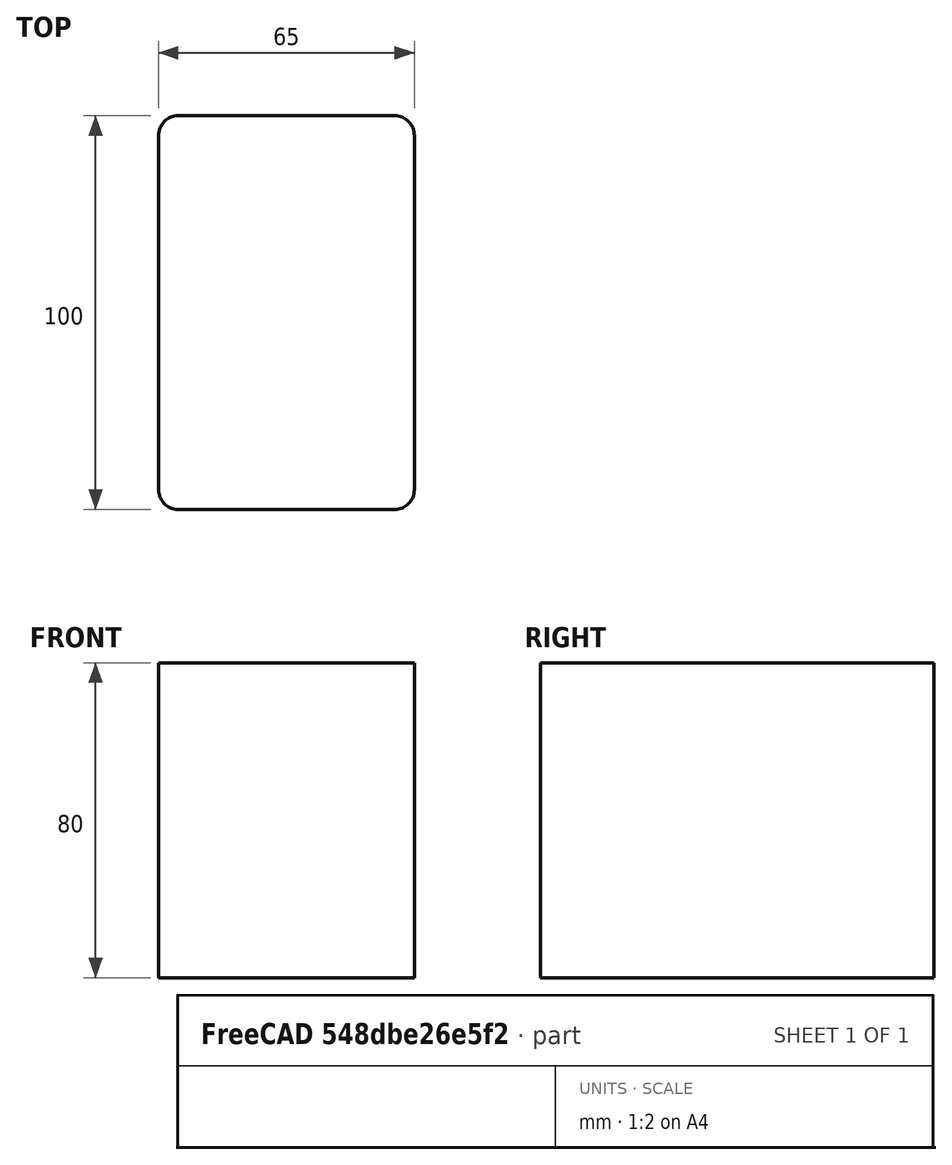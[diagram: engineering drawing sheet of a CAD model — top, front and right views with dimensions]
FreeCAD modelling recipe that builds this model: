
FCSTD DOCUMENT  (FreeCAD 0.22R37841 (Git))
Label: PrintheadCover
License: All rights reserved
LicenseURL: http://en.wikipedia.org/wiki/All_rights_reserved
objects: Mesh::Feature×8, Sketcher::SketchObject×2, PartDesign::Pad×1, PartDesign::Body×1
note: 5 computed .brp shape members not serialized (recipe doc carries the construction recipe); baked Part::Feature solids carry a one-line shape summary decoded from their .brp

FEATURE [Sketcher::SketchObject] Sketch
  AttachmentSupport = -> [XY_Plane]
  FullyConstrained = true
  MapMode = 5
  sketch-geometry (12):
    g0: LineSegment StartX=-32.5 StartY=45 StartZ=0 EndX=-32.5 EndY=-45 EndZ=0
    g1: LineSegment StartX=-27.5 StartY=-50 StartZ=0 EndX=27.5 EndY=-50 EndZ=0
    g2: LineSegment StartX=32.5 StartY=-45 StartZ=0 EndX=32.5 EndY=45 EndZ=0
    g3: LineSegment StartX=27.5 StartY=50 StartZ=0 EndX=-27.5 EndY=50 EndZ=0
    g4: ArcOfCircle CenterX=-27.5 CenterY=45 CenterZ=0 NormalX=0 NormalY=0 NormalZ=1 AngleXU=0 Radius=5 StartAngle=1.5708 EndAngle=3.14159
    g5: GeomPoint X=-32.5 Y=50 Z=0
    g6: ArcOfCircle CenterX=-27.5 CenterY=-45 CenterZ=0 NormalX=0 NormalY=0 NormalZ=1 AngleXU=0 Radius=5 StartAngle=3.14159 EndAngle=4.71239
    g7: GeomPoint X=-32.5 Y=-50 Z=0
    g8: ArcOfCircle CenterX=27.5 CenterY=-45 CenterZ=0 NormalX=0 NormalY=0 NormalZ=1 AngleXU=0 Radius=5 StartAngle=4.71239 EndAngle=6.28319
    g9: GeomPoint X=32.5 Y=-50 Z=0
    g10: ArcOfCircle CenterX=27.5 CenterY=45 CenterZ=0 NormalX=0 NormalY=0 NormalZ=1 AngleXU=0 Radius=5 StartAngle=4e-16 EndAngle=1.5708
    g11: GeomPoint X=32.5 Y=50 Z=0
  constraints (26):
    c: Vertical(g2)
    c: Horizontal(g1)
    c: Symmetric(g5,g11,g-2)
    c: Symmetric(g5,g7,g-1)
    c: PointOnObject(g5,g3)
    c: PointOnObject(g5,g0)
    c: Tangent(g3,g4) = -1.5708
    c: Tangent(g0,g4) = -1.5708
    c: PointOnObject(g7,g0)
    c: PointOnObject(g7,g1)
    c: Tangent(g0,g6) = -1.5708
    c: Tangent(g1,g6) = -1.5708
    c: PointOnObject(g9,g2)
    c: PointOnObject(g9,g1)
    c: Tangent(g2,g8) = -1.5708
    c: Tangent(g1,g8) = -1.5708
    c: PointOnObject(g11,g3)
    c: PointOnObject(g11,g2)
    c: Tangent(g3,g10) = -1.5708
    c: Tangent(g2,g10) = -1.5708
    c: Radius(g4) = 5
    c: Radius(g10) = 5
    c: Radius(g8) = 5
    c: Radius(g6) = 5
    c: Distance(g1,g3) = 100
    c: Distance(g2,g0) = 65
FEATURE [PartDesign::Pad] Pad
  Direction = (0,0,1)
  Length = 80
  Length2 = 10
  Profile = -> Sketch
  ReferenceAxis = -> Sketch [N_Axis]
  Suppressed = false
  Type = 0
FEATURE [Sketcher::SketchObject] Sketch001
  AttachmentSupport = -> [Pad]
  FullyConstrained = false
  MapMode = 5
  Placement = pos=(-32.5,2.6e-15,0) rot=(0.57735,-0.57735,-0.57735;2.0944rad)
  sketch-geometry (15):
    g0: Circle CenterX=16.7417 CenterY=44.3912 CenterZ=0 NormalX=0 NormalY=0 NormalZ=1 AngleXU=0 Radius=16.25
    g1: Circle CenterX=-3.2583 CenterY=20.8912 CenterZ=0 NormalX=0 NormalY=0 NormalZ=1 AngleXU=0 Radius=2.15
    g2: Circle CenterX=34.4683 CenterY=63.1422 CenterZ=0 NormalX=0 NormalY=0 NormalZ=1 AngleXU=0 Radius=2.15
    g3: LineSegment StartX=16.7417 StartY=44.3912 StartZ=0 EndX=16.4683 EndY=63.1422 EndZ=0
    g4: LineSegment StartX=16.4683 StartY=63.1422 StartZ=0 EndX=34.4683 EndY=63.1422 EndZ=0
    g5: LineSegment StartX=41.5605 StartY=20.9552 StartZ=0 EndX=41.5605 EndY=38.4552 EndZ=0
    g6: LineSegment StartX=41.5605 StartY=38.4552 StartZ=0 EndX=40.1436 EndY=38.4552 EndZ=0
    g7: ArcOfCircle CenterX=16.7417 CenterY=44.3912 CenterZ=0 NormalX=0 NormalY=0 NormalZ=1 AngleXU=0 Radius=23.5 StartAngle=6.09115 EndAngle=10.9217
    g8: LineSegment StartX=15.0081 StartY=20.9552 StartZ=0 EndX=41.5605 EndY=20.9552 EndZ=0
    g9: ArcOfCircle CenterX=16.7417 CenterY=44.3912 CenterZ=0 NormalX=0 NormalY=0 NormalZ=1 AngleXU=0 Radius=23.5 StartAngle=6.05577 EndAngle=6.09115
    g10: ArcOfCircle CenterX=40.1436 CenterY=38.9756 CenterZ=0 NormalX=0 NormalY=0 NormalZ=1 AngleXU=0 Radius=0.5204 StartAngle=2.91418 EndAngle=4.71239
    g11: LineSegment StartX=16.7417 StartY=44.3912 StartZ=0 EndX=-3.2583 EndY=44.3912 EndZ=0
    g12: LineSegment StartX=-3.2583 StartY=44.3912 StartZ=0 EndX=-3.2583 EndY=20.8912 EndZ=0
    g13: LineSegment StartX=-3.2583 StartY=20.8912 StartZ=0 EndX=-3.2583 EndY=18.7412 EndZ=0
    g14: LineSegment StartX=15.0081 StartY=20.9552 StartZ=0 EndX=18.2963 EndY=67.8397 EndZ=0
  constraints (29):
    c: Diameter(g0) = 32.5
    c: Coincident(g7,g0)
    c: Diameter(g1) = 4.3
    c: Diameter(g2) = 4.3
    c: Coincident(g8,g5)
    c: Vertical(g5)
    c: Distance(g5) = 17.5
    c: Coincident(g6,g5)
    c: Horizontal(g6)
    c: Diameter(g7) = 47
    c: Equal(g7,g9)
    c: Coincident(g7,g9)
    c: Tangent(g9,g10) = 1.5708
    c: Tangent(g6,g10) = 1.5708
    c: Horizontal(g11)
    c: Horizontal(g8)
    c: Coincident(g3,g11)
    c: Coincident(g12,g11)
    c: Coincident(g3,g0)
    c: Distance(g13) = 2.15
    c: Vertical(g13)
    c: Coincident(g13,g1)
    c: Coincident(g7,g8)
    c: Coincident(g1,g12)
    c: Distance(g11) = 20
    c: Vertical(g12)
    c: Distance(g12) = 23.5
    c: Coincident(g14,g7)
    c: PointOnObject(g14,g7)
FEATURE [PartDesign::Body] Body
  AllowCompound = false
  Group = -> [Sketch,Pad,Sketch001]
  Origin = -> Origin
  Tip = -> Pad
FEATURE [Mesh::Feature] Radial_Fan_5015
  Placement = pos=(-32,-22.4,-12.5) rot=(0,1,0;-1.5708rad)
FEATURE [Mesh::Feature] duct_left_v0
  Placement = pos=(-50,-29,-32) rot=(0,1,0;1.5708rad)
FEATURE [Mesh::Feature] Extruder_Assembly
  Placement = pos=(-23,-74,-41) rot=(1,0,0;-1.5708rad)
FEATURE [Mesh::Feature] Original_casing_
  Placement = pos=(0,0,-46) rot=(1,0,0;-1.5708rad)
FEATURE [Mesh::Feature] duct_right_v0
  Placement = pos=(32,-32,-11) rot=(0,1,0;1.5708rad)
FEATURE [Mesh::Feature] Radial_Fan_5016
  Placement = pos=(34,-23.6,-12.5) rot=(0,1,0;1.5708rad)
FEATURE [Mesh::Feature] _5mm_40mm_shroudV8_2  label="25mm-40mm shroudV8-2"
  Placement = pos=(4,-51,-3.8) rot=(0,0,1;0rad)
FEATURE [Mesh::Feature] _0mmFan  label="40mmFan"
  Placement = pos=(-5697,-51,15.3) rot=(0,0,1;0rad)
